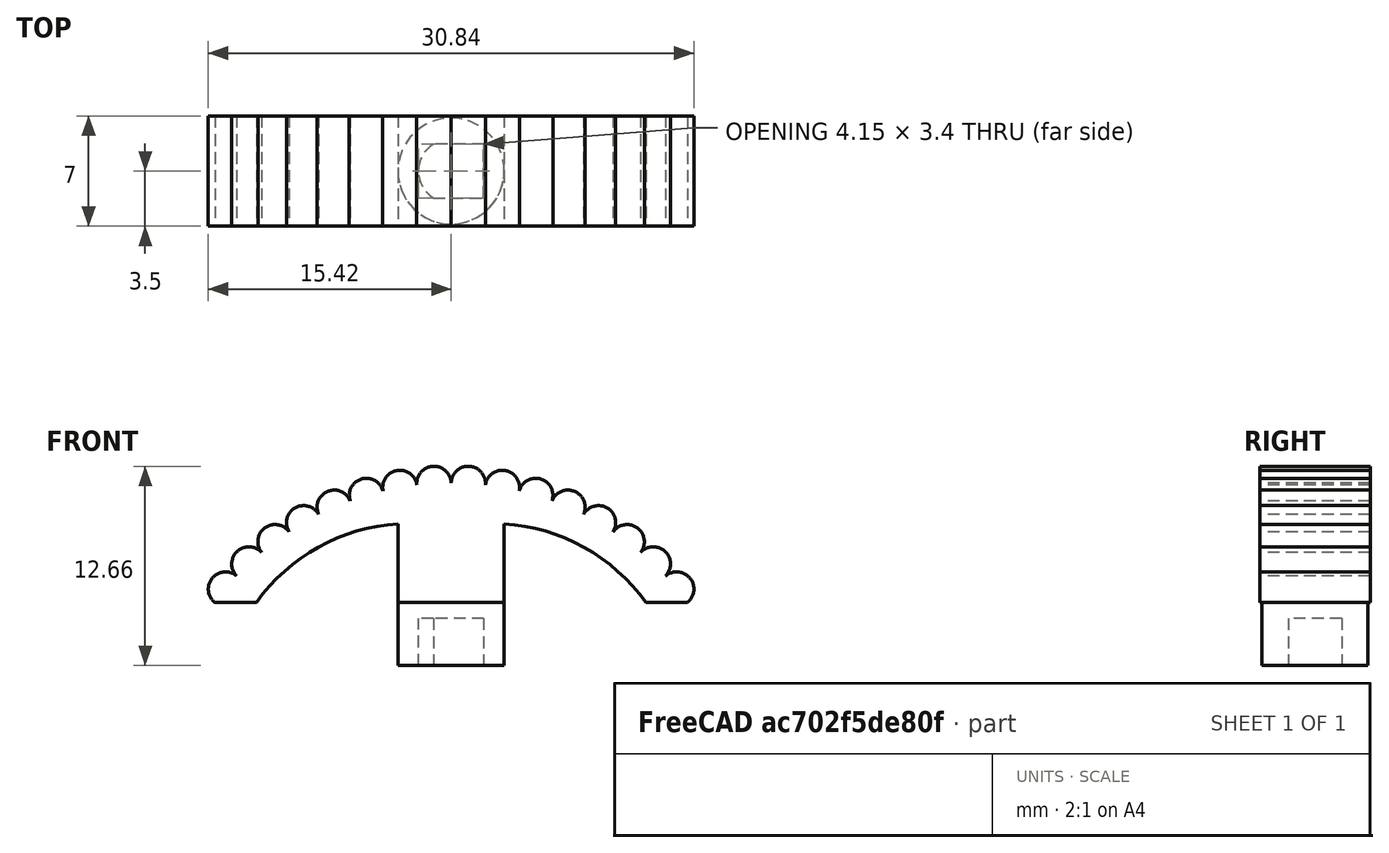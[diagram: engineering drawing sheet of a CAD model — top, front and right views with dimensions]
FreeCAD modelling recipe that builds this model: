
FCSTD DOCUMENT  (FreeCAD 0.20R28671 (Git))
Label: rueda pitch
License: All rights reserved
LicenseURL: http://en.wikipedia.org/wiki/All_rights_reserved
objects: TechDraw::DrawViewDimension×11, Sketcher::SketchObject×6, TechDraw::DrawViewAnnotation×6, PartDesign::Pocket×2, PartDesign::Pad×2, TechDraw::DrawViewSection×2, TechDraw::DrawLeaderLine×2, PartDesign::Revolution×1, PartDesign::Mirrored×1, PartDesign::Body×1, TechDraw::DrawSVGTemplate×1, Part::Refine×1, TechDraw::DrawProjGroupItem×1, TechDraw::DrawProjGroup×1, TechDraw::DrawViewSymbol×1, TechDraw::DrawPage×1
note: 19 computed .brp shape members not serialized (recipe doc carries the construction recipe); baked Part::Feature solids carry a one-line shape summary decoded from their .brp

FEATURE [Sketcher::SketchObject] Sketch
  FullyConstrained = true
  MapMode = 5
  Placement = pos=(0,0,0) rot=(1,0,0;1.5708rad)
  Support = -> [XZ_Plane]
  sketch-geometry (6):
    g0: LineSegment StartX=0 StartY=0 StartZ=0 EndX=-3.37 EndY=0 EndZ=0
    g1: LineSegment StartX=-3.37 StartY=0 StartZ=0 EndX=-3.37 EndY=3 EndZ=0
    g2: LineSegment StartX=-3.37 StartY=3 StartZ=0 EndX=0 EndY=3 EndZ=0
    g3: LineSegment StartX=0 StartY=3 StartZ=0 EndX=0 EndY=0 EndZ=0
    g4: LineSegment StartX=0 StartY=0 StartZ=0 EndX=3.37 EndY=0 EndZ=0
    g5: LineSegment StartX=0 StartY=3 StartZ=0 EndX=0 EndY=0 EndZ=0
  constraints (16):
    c: Coincident(g0,g-1)
    c: PointOnObject(g0,g-1)
    c: Coincident(g1,g0)
    c: Vertical(g1)
    c: Coincident(g2,g1)
    c: PointOnObject(g2,g-2)
    c: Horizontal(g2)
    c: Coincident(g3,g2)
    c: Coincident(g3,g0)
    c: Coincident(g4,g0)
    c: PointOnObject(g4,g-1)
    c: Equal(g4,g0)
    c: DistanceX(g0,g4) = 6.74
    c: DistanceY(g1,g1) = 3
    c: Coincident(g5,g2)
    c: Coincident(g5,g0)
FEATURE [PartDesign::Revolution] Revolution
  Angle = 360
  Axis = (0,2e-16,1)
  Base = (0,0,0)
  Placement = pos=(0,0,0) rot=(1,0,0;1.5708rad)
  Profile = -> Sketch
  ReferenceAxis = -> Sketch [V_Axis]
FEATURE [Sketcher::SketchObject] Sketch001
  FullyConstrained = true
  MapMode = 5
  Placement = pos=(0,1.3e-15,3) rot=(0,0,1;3.14159rad)
  Support = -> [Revolution]
  sketch-geometry (7):
    g0: LineSegment StartX=-2.075 StartY=1.7 StartZ=0 EndX=1.12857 EndY=1.7 EndZ=0
    g1: LineSegment StartX=1.12857 StartY=-1.7 StartZ=0 EndX=-2.075 EndY=-1.7 EndZ=0
    g2: LineSegment StartX=-2.075 StartY=-1.7 StartZ=0 EndX=-2.075 EndY=1.7 EndZ=0
    g3: ArcOfCircle CenterX=0.075 CenterY=0 CenterZ=0 NormalX=0 NormalY=0 NormalZ=1 AngleXU=0 Radius=2 StartAngle=5.2672 EndAngle=7.29917
    g4: GeomPoint X=2.075 Y=0 Z=0
    g5: LineSegment StartX=-2.075 StartY=0 StartZ=0 EndX=0 EndY=0 EndZ=0
    g6: LineSegment StartX=2.075 StartY=0 StartZ=0 EndX=0 EndY=0 EndZ=0
  constraints (20):
    c: Coincident(g1,g2)
    c: Coincident(g2,g0)
    c: Horizontal(g0)
    c: Horizontal(g1)
    c: Vertical(g2)
    c: Coincident(g3,g0)
    c: Coincident(g3,g1)
    c: Vertical(g0,g1)
    c: PointOnObject(g4,g3)
    c: Horizontal(g4,g3)
    c: PointOnObject(g5,g2)
    c: Coincident(g6,g4)
    c: Coincident(g6,g5)
    c: Equal(g6,g5)
    c: Horizontal(g5)
    c: Horizontal(g6)
    c: DistanceX(g5,g4) = 4.15
    c: DistanceY(g1,g0) = 3.4
    c: Coincident(g5,g-1)
    c: Radius(g3) = 2
FEATURE [PartDesign::Pocket] Pocket
  BaseFeature = -> Revolution
  Direction = (1,1,1)
  Length = 5
  Length2 = 100
  Placement = pos=(0,0,0) rot=(1,0,0;1.5708rad)
  Profile = -> Sketch001
  Type = 1
FEATURE [Sketcher::SketchObject] Sketch002
  ExternalGeometry = -> [Pocket]
  FullyConstrained = true
  MapMode = 5
  Placement = pos=(0,1.3e-15,3) rot=(0,0,1;3.14159rad)
  Support = -> [Pocket]
  sketch-geometry (1):
    g0: Circle CenterX=0 CenterY=0 CenterZ=0 NormalX=0 NormalY=0 NormalZ=1 AngleXU=0 Radius=3.37
  constraints (2):
    c: Coincident(g0,g-1)
    c: Equal(g0,g-3)
FEATURE [PartDesign::Pad] Pad
  BaseFeature = -> Pocket
  Direction = (0,1.1e-15,1)
  Length = 1
  Length2 = 100
  Placement = pos=(0,0,0) rot=(1,0,0;1.5708rad)
  Profile = -> Sketch002
  Type = 0
FEATURE [Sketcher::SketchObject] Sketch003
  ExternalGeometry = -> [Pad]
  FullyConstrained = true
  MapMode = 5
  Placement = pos=(0,0,0) rot=(1,0,0;1.5708rad)
  Support = -> [XZ_Plane]
  sketch-geometry (21):
    g0: LineSegment StartX=0 StartY=-7 StartZ=0 EndX=0 EndY=3 EndZ=0
    g1: ArcOfCircle CenterX=0 CenterY=-7 CenterZ=0 NormalX=0 NormalY=0 NormalZ=1 AngleXU=0 Radius=18.6011 StartAngle=0.632749 EndAngle=2.50884
    g2: LineSegment StartX=-15 StartY=4 StartZ=0 EndX=-15 EndY=4 EndZ=0
    g3: LineSegment StartX=-15 StartY=4 StartZ=0 EndX=15 EndY=4 EndZ=0
    g4: LineSegment StartX=15 StartY=4 StartZ=0 EndX=15 EndY=4 EndZ=0
    g5: ArcOfCircle CenterX=-14.3297 CenterY=4.86002 CenterZ=0 NormalX=0 NormalY=0 NormalZ=1 AngleXU=0 Radius=1.09039 StartAngle=0.850106 EndAngle=4.05033
    g6: ArcOfCircle CenterX=-12.8438 CenterY=6.45497 CenterZ=0 NormalX=0 NormalY=0 NormalZ=1 AngleXU=0 Radius=1.09039 StartAngle=0.73285 EndAngle=3.93307
    g7: ArcOfCircle CenterX=-11.1816 CenterY=7.86515 CenterZ=0 NormalX=0 NormalY=0 NormalZ=1 AngleXU=0 Radius=1.09039 StartAngle=0.615594 EndAngle=3.81581
    g8: ArcOfCircle CenterX=-9.36575 CenterY=9.07118 CenterZ=0 NormalX=0 NormalY=0 NormalZ=1 AngleXU=0 Radius=1.09039 StartAngle=0.498338 EndAngle=3.69856
    g9: ArcOfCircle CenterX=-7.42131 CenterY=10.0565 CenterZ=0 NormalX=0 NormalY=0 NormalZ=1 AngleXU=0 Radius=1.09039 StartAngle=0.381082 EndAngle=3.5813
    g10: ArcOfCircle CenterX=-5.37496 CenterY=10.8076 CenterZ=0 NormalX=0 NormalY=0 NormalZ=1 AngleXU=0 Radius=1.09039 StartAngle=0.263826 EndAngle=3.46405
    g11: ArcOfCircle CenterX=-3.25479 CenterY=11.3141 CenterZ=0 NormalX=0 NormalY=0 NormalZ=1 AngleXU=0 Radius=1.09039 StartAngle=0.14657 EndAngle=3.34679
    g12: ArcOfCircle CenterX=-1.08992 CenterY=11.5691 CenterZ=0 NormalX=0 NormalY=0 NormalZ=1 AngleXU=0 Radius=1.09039 StartAngle=0.029314 EndAngle=3.22953
    g13: ArcOfCircle CenterX=1.08992 CenterY=11.5691 CenterZ=0 NormalX=0 NormalY=0 NormalZ=1 AngleXU=0 Radius=1.09039 StartAngle=6.19524 EndAngle=9.39546
    g14: ArcOfCircle CenterX=3.25479 CenterY=11.3141 CenterZ=0 NormalX=0 NormalY=0 NormalZ=1 AngleXU=0 Radius=1.09039 StartAngle=6.07799 EndAngle=9.27821
    g15: ArcOfCircle CenterX=5.37496 CenterY=10.8076 CenterZ=0 NormalX=0 NormalY=0 NormalZ=1 AngleXU=0 Radius=1.09039 StartAngle=5.96073 EndAngle=9.16095
    g16: ArcOfCircle CenterX=7.42131 CenterY=10.0565 CenterZ=0 NormalX=0 NormalY=0 NormalZ=1 AngleXU=0 Radius=1.09039 StartAngle=5.84348 EndAngle=9.0437
    g17: ArcOfCircle CenterX=9.36575 CenterY=9.07118 CenterZ=0 NormalX=0 NormalY=0 NormalZ=1 AngleXU=0 Radius=1.09039 StartAngle=5.72622 EndAngle=8.92644
    g18: ArcOfCircle CenterX=11.1816 CenterY=7.86515 CenterZ=0 NormalX=0 NormalY=0 NormalZ=1 AngleXU=0 Radius=1.09039 StartAngle=5.60896 EndAngle=8.80918
    g19: ArcOfCircle CenterX=12.8438 CenterY=6.45497 CenterZ=0 NormalX=0 NormalY=0 NormalZ=1 AngleXU=0 Radius=1.09039 StartAngle=5.49171 EndAngle=8.69193
    g20: ArcOfCircle CenterX=14.3297 CenterY=4.86002 CenterZ=0 NormalX=0 NormalY=0 NormalZ=1 AngleXU=0 Radius=1.09039 StartAngle=5.37445 EndAngle=8.57467
  constraints (79):
    c: PointOnObject(g0,g-2)
    c: PointOnObject(g0,g-3)
    c: Vertical(g0)
    c: DistanceY(g0,g0) = 10
    c: Coincident(g1,g0)
    c: DistanceY(g-3,g1) = 1
    c: DistanceX(g1,g1) = 30
    c: Coincident(g2,g1)
    c: Vertical(g2)
    c: Coincident(g3,g2)
    c: Horizontal(g3)
    c: Coincident(g4,g3)
    c: Coincident(g4,g1)
    c: PointOnObject(g-4,g3)
    c: Vertical(g4)
    c: Coincident(g5,g2)
    c: PointOnObject(g5,g1)
    c: Coincident(g6,g5)
    c: PointOnObject(g6,g1)
    c: Coincident(g7,g6)
    c: PointOnObject(g7,g1)
    c: Coincident(g8,g7)
    c: PointOnObject(g8,g1)
    c: Coincident(g9,g8)
    c: PointOnObject(g9,g1)
    c: Coincident(g10,g9)
    c: PointOnObject(g10,g1)
    c: Coincident(g11,g10)
    c: PointOnObject(g11,g1)
    c: Coincident(g12,g11)
    c: PointOnObject(g12,g1)
    c: Coincident(g13,g12)
    c: PointOnObject(g13,g1)
    c: Coincident(g14,g13)
    c: PointOnObject(g14,g1)
    c: Coincident(g15,g14)
    c: PointOnObject(g15,g1)
    c: Coincident(g16,g15)
    c: PointOnObject(g16,g1)
    c: Coincident(g17,g16)
    c: PointOnObject(g17,g1)
    c: Coincident(g18,g17)
    c: PointOnObject(g18,g1)
    c: Coincident(g19,g18)
    c: PointOnObject(g19,g1)
    c: Coincident(g20,g19)
    c: Coincident(g20,g4)
    c: PointOnObject(g5,g1)
    c: PointOnObject(g6,g1)
    c: PointOnObject(g7,g1)
    c: PointOnObject(g8,g1)
    c: PointOnObject(g9,g1)
    c: PointOnObject(g10,g1)
    c: PointOnObject(g11,g1)
    c: PointOnObject(g12,g1)
    c: PointOnObject(g13,g1)
    c: PointOnObject(g14,g1)
    c: PointOnObject(g15,g1)
    c: PointOnObject(g16,g1)
    c: PointOnObject(g18,g1)
    c: PointOnObject(g19,g1)
    c: PointOnObject(g20,g1)
    c: Equal(g20,g19)
    c: Equal(g19,g18)
    c: Equal(g18,g16)
    c: Equal(g16,g15)
    c: Equal(g15,g14)
    c: Equal(g14,g13)
    c: Equal(g13,g12)
    c: Equal(g12,g11)
    c: Equal(g11,g10)
    c: Equal(g10,g9)
    c: Equal(g9,g8)
    c: Equal(g8,g7)
    c: Equal(g7,g6)
    c: Equal(g6,g5)
    c: PointOnObject(g17,g1)
    c: Equal(g17,g18)
    c: Horizontal(g4,g2)
FEATURE [PartDesign::Pad] Pad001
  BaseFeature = -> Pad
  Direction = (0,-1,-2e-16)
  Length = 7
  Length2 = 100
  Midplane = true
  Placement = pos=(0,0,0) rot=(1,0,0;1.5708rad)
  Profile = -> Sketch003
  Type = 0
FEATURE [Sketcher::SketchObject] Sketch004
  FullyConstrained = true
  MapMode = 5
  Placement = pos=(0,3.5,8e-16) rot=(-1,0,0;1.5708rad)
  Support = -> [Pad001]
FEATURE [Sketcher::SketchObject] Sketch005
  ExternalGeometry = -> [Pad001]
  FullyConstrained = true
  MapMode = 5
  Placement = pos=(0,3.5,8e-16) rot=(-1,0,0;1.5708rad)
  Support = -> [Pad001]
  sketch-geometry (3):
    g0: LineSegment StartX=-3.37 StartY=-4 StartZ=0 EndX=-3.37 EndY=-9 EndZ=0
    g1: ArcOfCircle CenterX=-2.60576 CenterY=2.97564 CenterZ=0 NormalX=0 NormalY=0 NormalZ=1 AngleXU=0 Radius=12 StartAngle=3.76192 EndAngle=4.64866
    g2: LineSegment StartX=-3.37 StartY=-4 StartZ=0 EndX=-12.37 EndY=-4 EndZ=0
  constraints (10):
    c: PointOnObject(g0,g-3)
    c: Coincident(g1,g0)
    c: PointOnObject(g1,g-3)
    c: Coincident(g2,g0)
    c: Coincident(g2,g1)
    c: DistanceX(g2,g2) = 9
    c: Vertical(g0)
    c: Vertical(g0,g-4)
    c: Radius(g1) = 12
    c: DistanceY(g0,g0) = 5
FEATURE [PartDesign::Pocket] Pocket001
  BaseFeature = -> Pad001
  Direction = (0,-1,-2e-16)
  Length = 5
  Length2 = 100
  Placement = pos=(0,0,0) rot=(1,0,0;1.5708rad)
  Profile = -> Sketch005
  Type = 1
FEATURE [PartDesign::Mirrored] Mirrored
  BaseFeature = -> Pocket001
  MirrorPlane = -> Sketch005 [V_Axis]
  Originals = -> [Pocket001]
  Overlap = 0
  Placement = pos=(0,0,0) rot=(1,0,0;1.5708rad)
FEATURE [PartDesign::Body] Body
  Group = -> [Sketch,Revolution,Sketch001,Pocket,Sketch002,Pad,Sketch003,Pad001,Sketch004,Sketch005,Pocket001,Mirrored]
  Origin = -> Origin
  Tip = -> Mirrored
FEATURE [TechDraw::DrawSVGTemplate] Template003
  EditableTexts = AUTHOR_NAME=Daniel García García; DATE=13-04-2022; DN=4; DOCUMENT_TYPE=Plano de pieza; PN=5; REVISION=1; SCALE=4:1; SHEET=4/15; SIZE=A4; TITLELINE-1=Rueda de Pitch
  Height = 210
  Orientation = 1
  Width = 297
FEATURE [TechDraw::DrawViewAnnotation] Annotation
  Font = osifont
  LineSpace = 80
  LockPosition = false
  MaxWidth = -1
  Rotation = 0
  ScaleType = 0
  Text = Sección A-A'
  TextSize = 5
  TextStyle = 0
  X = 77.8202
  Y = 110.004
FEATURE [TechDraw::DrawViewAnnotation] Annotation001
  Font = osifont
  LineSpace = 80
  LockPosition = false
  MaxWidth = -1
  Rotation = 0
  ScaleType = 0
  Text = B
  TextSize = 5
  TextStyle = 0
  X = 51.8618
  Y = 142.258
FEATURE [TechDraw::DrawViewAnnotation] Annotation002
  Font = osifont
  LineSpace = 80
  LockPosition = false
  MaxWidth = -1
  Rotation = 0
  ScaleType = 0
  Text = B'
  TextSize = 5
  TextStyle = 0
  X = 100.653
  Y = 143.199
FEATURE [TechDraw::DrawViewAnnotation] Annotation003
  Font = osifont
  LineSpace = 80
  LockPosition = false
  MaxWidth = -1
  Rotation = 0
  ScaleType = 0
  Text = Sección B-B'
  TextSize = 5
  TextStyle = 0
  X = 75.9179
  Y = 27.6019
FEATURE [Part::Refine] Mirrored001
  Source = -> Mirrored
FEATURE [TechDraw::DrawProjGroupItem] ProjItem  label="Front"
  CoarseView = false
  Direction = (0,-1,0)
  Focus = 100
  HardHidden = false
  IsoCount = 0
  IsoHidden = false
  IsoVisible = false
  LockPosition = true
  Perspective = false
  Rotation = 0
  RotationVector = (1,0,0)
  Scale = 4
  ScaleType = 2
  SeamHidden = false
  SeamVisible = true
  SmoothHidden = false
  SmoothVisible = true
  Source = -> [Mirrored001]
  Type = 0
  X = 0
  XDirection = (1,0,0)
  Y = 0
FEATURE [TechDraw::DrawProjGroup] ProjGroup
  Anchor = -> Mirrored001
  AutoDistribute = false
  LockPosition = true
  ProjectionType = 0
  Rotation = 0
  Scale = 4
  ScaleType = 2
  Source = -> [Mirrored]
  Views = -> [ProjItem]
  X = 206.06
  Y = 142.493
  spacingX = 15
  spacingY = 15
FEATURE [TechDraw::DrawViewSection] SectionView  label="Section A - A"
  BaseView = -> ProjItem
  CoarseView = false
  CutSurfaceDisplay = 2
  Direction = (1,0,0)
  FileGeomPattern = <path>
  FileHatchPattern = <path>
  Focus = 100
  FuseBeforeCut = false
  HardHidden = false
  HatchScale = 1
  IsoCount = 0
  IsoHidden = false
  IsoVisible = false
  LockPosition = true
  NameGeomPattern = Diamond
  Perspective = false
  Rotation = 0
  Scale = 4
  ScaleType = 2
  SeamHidden = false
  SeamVisible = true
  SectionDirection = 1
  SectionNormal = (1,0,0)
  SectionOrigin = (0,0,6.33)
  SectionSymbol = A
  SmoothHidden = false
  SmoothVisible = true
  Source = -> [Mirrored]
  X = 75.8
  XDirection = (0,1,0)
  Y = 142.995
FEATURE [TechDraw::DrawLeaderLine] LeaderLine001
  AutoHorizontal = false
  EndSymbol = 7
  LeaderParent = -> SectionView
  LockPosition = true
  Rotation = 0
  Scalable = false
  ScaleType = 0
  StartSymbol = 0
  WayPoints = (2) [(6,4.82,0),(6,2.82,0)]
  X = -5.99471
  Y = -4.80217
FEATURE [TechDraw::DrawLeaderLine] LeaderLine
  AutoHorizontal = false
  EndSymbol = 7
  LeaderParent = -> SectionView
  LockPosition = true
  Rotation = 0
  Scalable = false
  ScaleType = 0
  StartSymbol = 0
  WayPoints = (2) [(6,4.82,0),(6,2.82,0)]
  X = 5.99376
  Y = -4.82106
FEATURE [TechDraw::DrawViewSection] SectionView001  label="Section B-B'"
  BaseView = -> SectionView
  CoarseView = false
  CutSurfaceDisplay = 2
  Direction = (0,0,1)
  FileGeomPattern = <path>
  FileHatchPattern = <path>
  Focus = 100
  FuseBeforeCut = false
  HardHidden = false
  HatchScale = 1
  IsoCount = 0
  IsoHidden = false
  IsoVisible = false
  LockPosition = true
  NameGeomPattern = Diamond
  Perspective = false
  Rotation = 0
  Scale = 4
  ScaleType = 2
  SeamHidden = false
  SeamVisible = true
  SectionDirection = 3
  SectionNormal = (0,0,1)
  SectionOrigin = (0,0,2.33)
  SectionSymbol = B-B'
  SmoothHidden = false
  SmoothVisible = true
  Source = -> [Mirrored]
  X = 75.8
  XDirection = (0,1,0)
  Y = 50.4292
FEATURE [TechDraw::DrawViewDimension] Dimension009
  AngleOverride = false
  Arbitrary = false
  ArbitraryTolerances = false
  EqualTolerance = true
  ExtensionAngle = 0
  FormatSpec = %.2w
  FormatSpecOverTolerance = %+.2w
  FormatSpecUnderTolerance = %+.2w
  Inverted = false
  LineAngle = 0
  LockPosition = false
  MeasureType = 1
  OverTolerance = 0
  References2D = -> [SectionView001]
  Rotation = 0
  ScaleType = 0
  TheoreticalExact = false
  Type = 2
  UnderTolerance = 0
  X = -33.0547
  Y = 0.607131
FEATURE [TechDraw::DrawViewDimension] Dimension010
  AngleOverride = false
  Arbitrary = false
  ArbitraryTolerances = false
  EqualTolerance = true
  ExtensionAngle = 0
  FormatSpec = %.2w
  FormatSpecOverTolerance = %+.2w
  FormatSpecUnderTolerance = %+.2w
  Inverted = false
  LineAngle = 0
  LockPosition = false
  MeasureType = 1
  OverTolerance = 0
  References2D = -> [SectionView001]
  Rotation = 0
  ScaleType = 0
  TheoreticalExact = false
  Type = 1
  UnderTolerance = 0
  X = 0.514799
  Y = 26.5766
FEATURE [TechDraw::DrawViewDimension] Dimension011
  AngleOverride = false
  Arbitrary = false
  ArbitraryTolerances = false
  EqualTolerance = true
  ExtensionAngle = 0
  FormatSpec = R%.2w
  FormatSpecOverTolerance = %+.2w
  FormatSpecUnderTolerance = %+.2w
  Inverted = false
  LineAngle = 0
  LockPosition = false
  MeasureType = 1
  OverTolerance = 0
  References2D = -> [SectionView001]
  Rotation = 0
  ScaleType = 0
  TheoreticalExact = false
  Type = 4
  UnderTolerance = 0
  X = 20.3016
  Y = 19.7377
FEATURE [TechDraw::DrawViewDimension] Dimension012
  AngleOverride = false
  Arbitrary = false
  ArbitraryTolerances = false
  EqualTolerance = true
  ExtensionAngle = 0
  FormatSpec = ⌀%.2w
  FormatSpecOverTolerance = %+.2w
  FormatSpecUnderTolerance = %+.2w
  Inverted = false
  LineAngle = 0
  LockPosition = false
  MeasureType = 1
  OverTolerance = 0
  References2D = -> [SectionView001]
  Rotation = 0
  ScaleType = 0
  TheoreticalExact = false
  Type = 5
  UnderTolerance = 0
  X = 31.8764
  Y = -3.70655
FEATURE [TechDraw::DrawViewDimension] Dimension016
  AngleOverride = false
  Arbitrary = false
  ArbitraryTolerances = false
  EqualTolerance = true
  ExtensionAngle = 0
  FormatSpec = %.2w
  FormatSpecOverTolerance = %+.2w
  FormatSpecUnderTolerance = %+.2w
  Inverted = false
  LineAngle = 0
  LockPosition = false
  MeasureType = 1
  OverTolerance = 0
  References2D = -> [ProjItem]
  Rotation = 0
  ScaleType = 0
  TheoreticalExact = false
  Type = 1
  UnderTolerance = 0
  X = -6.43499
  Y = -27.6101
FEATURE [TechDraw::DrawViewDimension] Dimension017
  AngleOverride = false
  Arbitrary = false
  ArbitraryTolerances = false
  EqualTolerance = true
  ExtensionAngle = 0
  FormatSpec = R%.2w
  FormatSpecOverTolerance = %+.2w
  FormatSpecUnderTolerance = %+.2w
  Inverted = false
  LineAngle = 0
  LockPosition = false
  MeasureType = 1
  OverTolerance = 0
  References2D = -> [ProjItem]
  Rotation = 0
  ScaleType = 0
  TheoreticalExact = false
  Type = 4
  UnderTolerance = 0
  X = -29.6524
  Y = -4.32431
FEATURE [TechDraw::DrawViewDimension] Dimension018
  AngleOverride = false
  Arbitrary = false
  ArbitraryTolerances = false
  EqualTolerance = true
  ExtensionAngle = 0
  FormatSpec = %.2w
  FormatSpecOverTolerance = %+.2w
  FormatSpecUnderTolerance = %+.2w
  Inverted = false
  LineAngle = 0
  LockPosition = false
  MeasureType = 1
  OverTolerance = 0
  References2D = -> [ProjItem]
  Rotation = 0
  ScaleType = 0
  TheoreticalExact = false
  Type = 2
  UnderTolerance = 0
  X = -48.9832
  Y = -15.5329
FEATURE [TechDraw::DrawViewDimension] Dimension019
  AngleOverride = false
  Arbitrary = false
  ArbitraryTolerances = false
  EqualTolerance = true
  ExtensionAngle = 0
  FormatSpec = %.2w
  FormatSpecOverTolerance = %+.2w
  FormatSpecUnderTolerance = %+.2w
  Inverted = false
  LineAngle = 0
  LockPosition = false
  MeasureType = 1
  OverTolerance = 0
  References2D = -> [SectionView]
  Rotation = 0
  ScaleType = 0
  TheoreticalExact = false
  Type = 2
  UnderTolerance = 0
  X = 30.4808
  Y = -18.106
FEATURE [TechDraw::DrawViewDimension] Dimension020
  AngleOverride = false
  Arbitrary = false
  ArbitraryTolerances = false
  EqualTolerance = true
  ExtensionAngle = 0
  FormatSpec = %.2w
  FormatSpecOverTolerance = %+.2w
  FormatSpecUnderTolerance = %+.2w
  Inverted = false
  LineAngle = 0
  LockPosition = false
  MeasureType = 1
  OverTolerance = 0
  References2D = -> [SectionView]
  Rotation = 0
  ScaleType = 0
  TheoreticalExact = false
  Type = 2
  UnderTolerance = 0
  X = -38.7077
  Y = -15.3338
FEATURE [TechDraw::DrawViewDimension] Dimension
  AngleOverride = false
  Arbitrary = false
  ArbitraryTolerances = false
  EqualTolerance = true
  ExtensionAngle = 0
  FormatSpec = %.2w
  FormatSpecOverTolerance = %+.2w
  FormatSpecUnderTolerance = %+.2w
  Inverted = false
  LineAngle = 0
  LockPosition = false
  MeasureType = 1
  OverTolerance = 0
  References2D = -> [SectionView]
  Rotation = 0
  ScaleType = 0
  TheoreticalExact = false
  Type = 1
  UnderTolerance = 0
  X = 0.257399
  Y = 38.8872
FEATURE [TechDraw::DrawViewDimension] Dimension021
  AngleOverride = false
  Arbitrary = false
  ArbitraryTolerances = false
  EqualTolerance = true
  ExtensionAngle = 0
  FormatSpec = %.2w
  FormatSpecOverTolerance = %+.2w
  FormatSpecUnderTolerance = %+.2w
  Inverted = false
  LineAngle = 0
  LockPosition = false
  MeasureType = 1
  OverTolerance = 0
  References2D = -> [ProjItem]
  Rotation = 0
  ScaleType = 0
  TheoreticalExact = false
  Type = 1
  UnderTolerance = 0
  X = -22.3938
  Y = 7.57647
FEATURE [TechDraw::DrawViewAnnotation] Annotation004
  Font = osifont
  LineSpace = 80
  LockPosition = false
  MaxWidth = -1
  Rotation = 0
  ScaleType = 0
  Text = Default Text
  TextSize = 5
  TextStyle = 0
  X = 150.353
  Y = 65.7723
FEATURE [TechDraw::DrawViewSymbol] Symbol
  LockPosition = false
  Rotation = 0
  Scale = 0.3
  ScaleType = 2
  Symbol = <blob: 2444 chars omitted>
  X = 217.487
  Y = 36.9001
FEATURE [TechDraw::DrawViewAnnotation] Annotation005
  Font = osifont
  LineSpace = 80
  LockPosition = false
  MaxWidth = -1
  Rotation = 0
  ScaleType = 0
  Text = '
  TextSize = 5
  TextStyle = 0
  X = 207.932
  Y = 97.189
FEATURE [TechDraw::DrawPage] Page003  label="Rueda Pitch"
  KeepUpdated = true
  NextBalloonIndex = 1
  ProjectionType = 0
  Template = -> Template003
  Views = -> [ProjGroup,SectionView,LeaderLine001,LeaderLine,Annotation,Annotation001,Annotation002,Annotation003,SectionView001,Dimension009,Dimension010,Dimension011,Dimension012,Dimension016,Dimension017,Dimension018,Dimension019,Dimension020,Dimension,Dimension021,Symbol,Annotation005]
note: 4 file-system paths scrubbed to <path> (originals preserved in the JSON sidecar)
